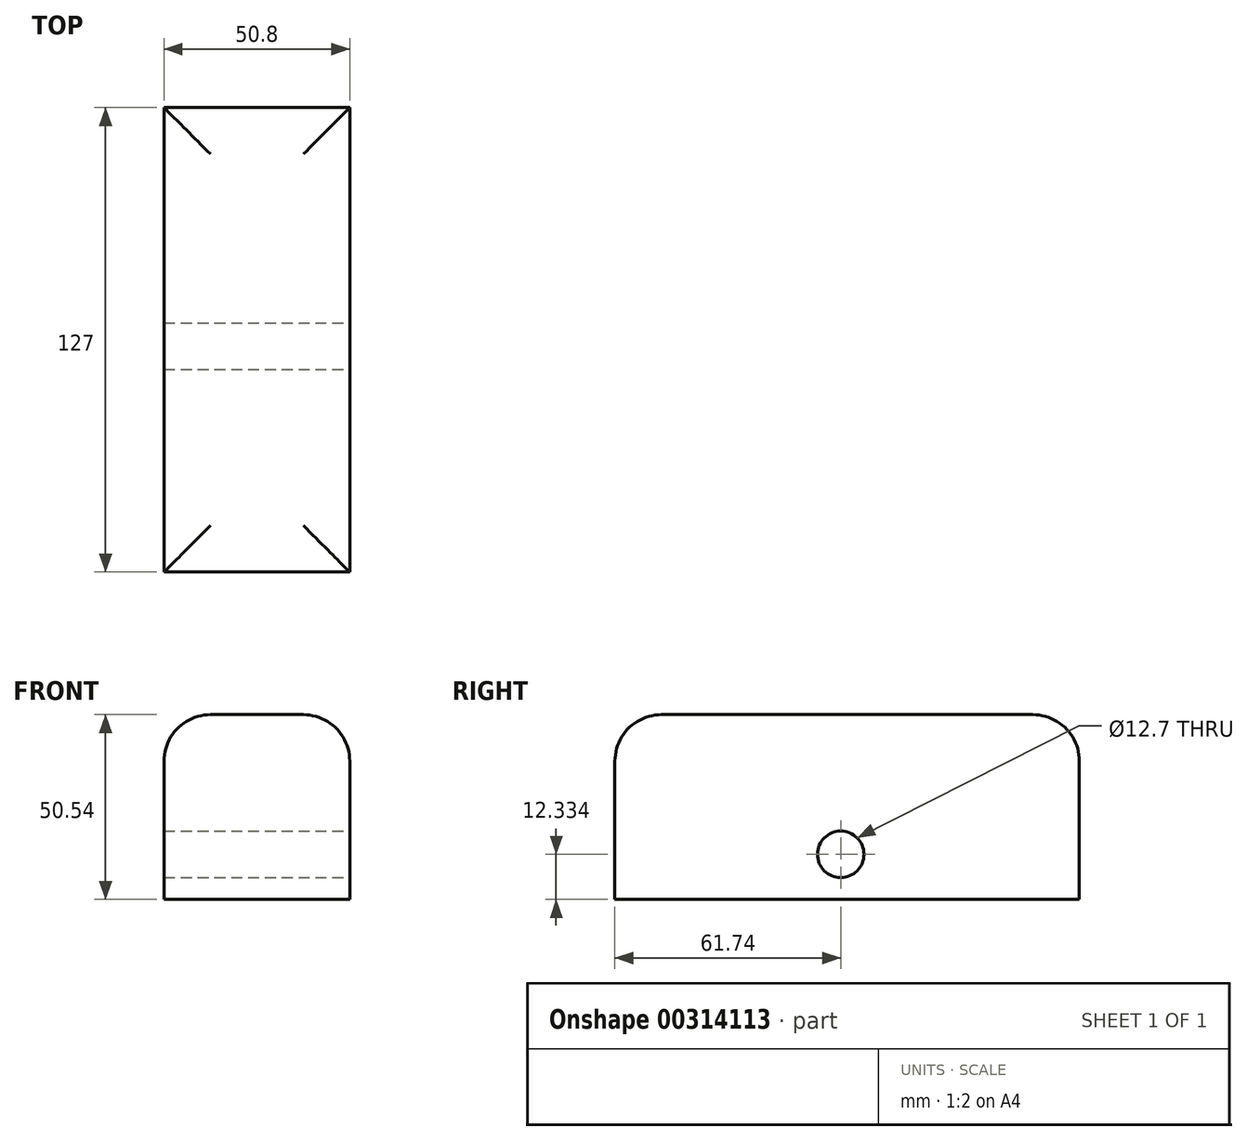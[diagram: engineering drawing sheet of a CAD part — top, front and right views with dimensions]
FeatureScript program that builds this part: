
annotation { "Feature Type Name" : "Feature", "Feature Type Description" : "" }
export const myFeature = defineFeature(function(context is Context, id is Id, definition is map)
    precondition{}
    {
        {
            var Q0;
            Q0=qCreatedBy(makeId("Top.planeOp"),FACE);
            var sketch = newSketch(context, id + "F0", { "sketchPlane" : qUnion([Q0])});
            skLineSegment(sketch, "E0.bottom", {"start": v(-25.4, 65.26) * mm, "end": v(25.4, 65.26) * mm});
            skLineSegment(sketch, "E0.top", {"start": v(-25.4, -61.74) * mm, "end": v(25.4, -61.74) * mm});
            skLineSegment(sketch, "E0.left", {"start": v(-25.4, 65.26) * mm, "end": v(-25.4, -61.74) * mm});
            skLineSegment(sketch, "E0.right", {"start": v(25.4, 65.26) * mm, "end": v(25.4, -61.74) * mm});
            skSolve(sketch);
        }
        {
            var Q0;
            Q0 = qSketchRegion(id + "F0", true);
            extrude(context, id + "F1", {"entities" : qUnion([Q0]), "depth" : 50.54 * mm});
        }
        {
            var Q0;
            Q0=makeQuery(id+"F1.opExtrude","CAP_EDGE",EDGE,{"disambiguationData":[OSD([sQuery(id+"F0.wireOp",EDGE,"E0.right")])],"isStart":false});
            var Q1;
            Q1=makeQuery(id+"F1.opExtrude","CAP_EDGE",EDGE,{"disambiguationData":[OSD([sQuery(id+"F0.wireOp",EDGE,"E0.top")])],"isStart":false});
            var Q2;
            Q2=makeQuery(id+"F1.opExtrude","CAP_EDGE",EDGE,{"disambiguationData":[OSD([sQuery(id+"F0.wireOp",EDGE,"E0.left")])],"isStart":false});
            var Q3;
            Q3=makeQuery(id+"F1.opExtrude","CAP_EDGE",EDGE,{"disambiguationData":[OSD([sQuery(id+"F0.wireOp",EDGE,"E0.bottom")])],"isStart":false});
            fillet(context, id + "F2", {"entities" : qUnion([Q0, Q1, Q2, Q3]), "radius" : 12.7 * mm, "tangentPropagation" : true, "allowEdgeOverflow" : false});
        }
        {
            var Q0;
            Q0=makeQuery(id+"F1.opExtrude","SWEPT_FACE",FACE,{"disambiguationData":[OSD([sQuery(id+"F0.wireOp",EDGE,"E0.right")])]});
            var sketch = newSketch(context, id + "F3", { "sketchPlane" : qUnion([Q0])});
            skCircle(sketch, "E1", {"center": v(0, 12.33) * mm, "radius": 6.35 * mm});
            skSolve(sketch);
        }
        {
            var Q0;
            Q0 = qSketchRegion(id + "F3", true);
            extrude(context, id + "F4", {"entities" : qUnion([Q0]), "operationType" : NewBodyOperationType.REMOVE, "oppositeDirection" : true, "depth" : 105.58 * mm});
        }
    });
